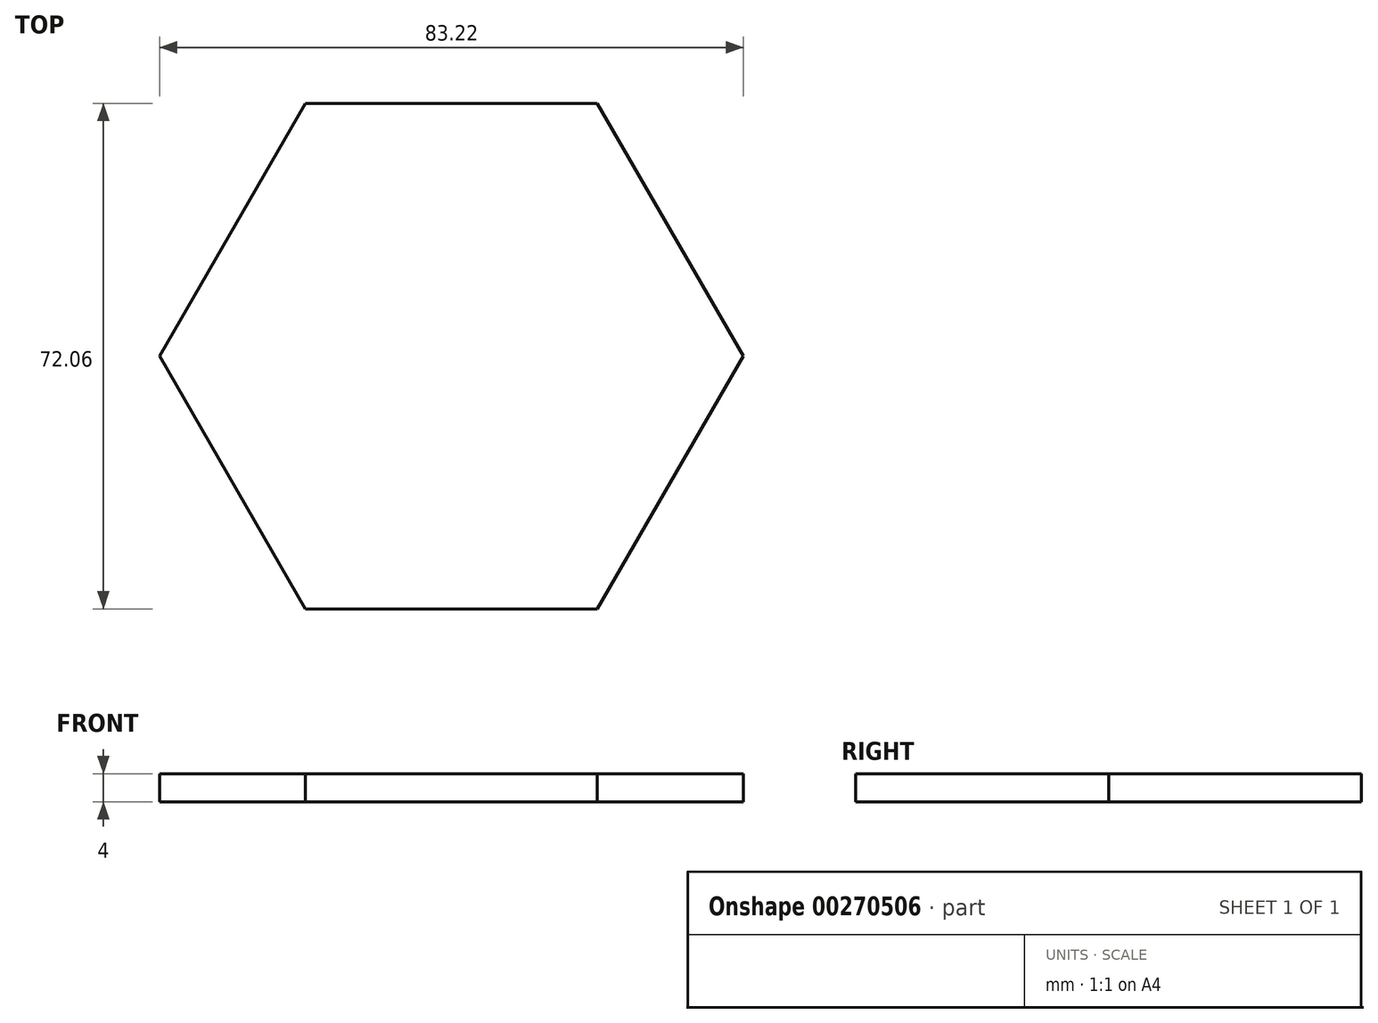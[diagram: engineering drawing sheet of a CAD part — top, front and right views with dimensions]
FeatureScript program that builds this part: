
annotation { "Feature Type Name" : "Feature", "Feature Type Description" : "" }
export const myFeature = defineFeature(function(context is Context, id is Id, definition is map)
    precondition{}
    {
        {
            var Q0;
            Q0=qCreatedBy(makeId("Top.planeOp"),FACE);
            var sketch = newSketch(context, id + "F0", { "sketchPlane" : qUnion([Q0])});
            skCircle(sketch, "E0.cCircle", {"center": v(0, 0) * mm, "radius": 36.03 * mm, "construction": true});
            skLineSegment(sketch, "E0.0", {"start": v(-20.8, 36.03) * mm, "end": v(20.8, 36.03) * mm});
            skLineSegment(sketch, "E0.1", {"start": v(20.8, 36.03) * mm, "end": v(41.6, 0) * mm});
            skLineSegment(sketch, "E0.2", {"start": v(41.6, 0) * mm, "end": v(20.8, -36.03) * mm});
            skLineSegment(sketch, "E0.3", {"start": v(20.8, -36.03) * mm, "end": v(-20.8, -36.03) * mm});
            skLineSegment(sketch, "E0.4", {"start": v(-20.8, -36.03) * mm, "end": v(-41.6, 0) * mm});
            skLineSegment(sketch, "E0.5", {"start": v(-41.6, 0) * mm, "end": v(-20.8, 36.03) * mm});
            skPoint(sketch, "E0.0.midPoint", {"position": v(0, 36.03) * mm});
            skSolve(sketch);
        }
        {
            var Q0;
            Q0 = qSketchRegion(id + "F0", true);
            extrude(context, id + "F1", {"entities" : qUnion([Q0]), "depth" : 4 * mm});
        }
    });
